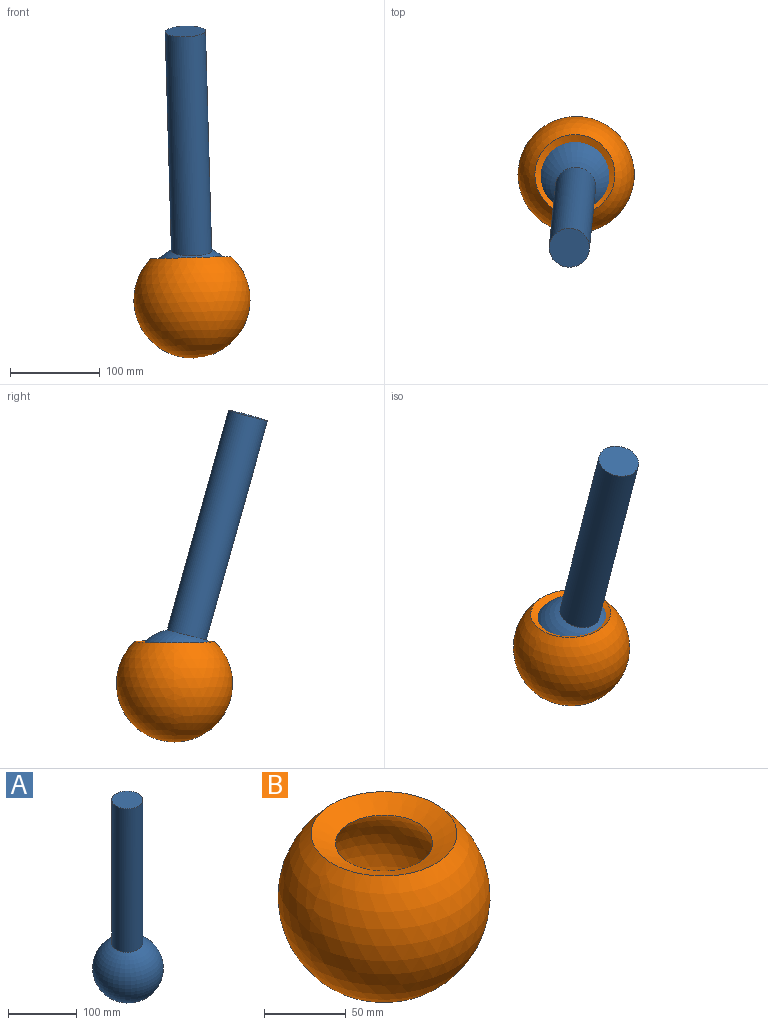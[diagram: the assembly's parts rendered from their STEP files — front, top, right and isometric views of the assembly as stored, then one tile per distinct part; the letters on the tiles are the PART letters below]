
ASSEMBLY  parts=2 mates=1
PART A: 3 faces, bbox 75.3x45x350 mm
  f0: plane 45x45mm, normal (0,0,1), area 1590.4mm2, adj f1
  f1: cylinder r=22.5mm len=255.35mm, axis (0,0,1), area 36001.2mm2, adj f0,f2
  f2: torus R=1.4mm, axis (-0.03,0,1), area 31142.1mm2, adj f1
PART B: 3 faces, bbox 130x130x112.2 mm
  f0: sphere r=65mm, area 45807.1mm2, adj f2
  f1: sphere r=50mm, area 28330.6mm2, adj f2
  f2: cone r=29.76mm half-angle=65deg, axis (0,0,1), area 3865.9mm2, adj f0,f1
PLACE A rot(axis=(0.09,0.13,-0.99),123.9deg) t=(-36.72,-154.14,278.92)mm
PLACE B rot(axis=(0,-1,0),1.6deg) t=(-37.35,-152.55,267.94)mm fixed
MATE ball B.f2 <-> A.f2  axis (-0.03,0,1) through (-37.35,-152.55,267.94)mm
